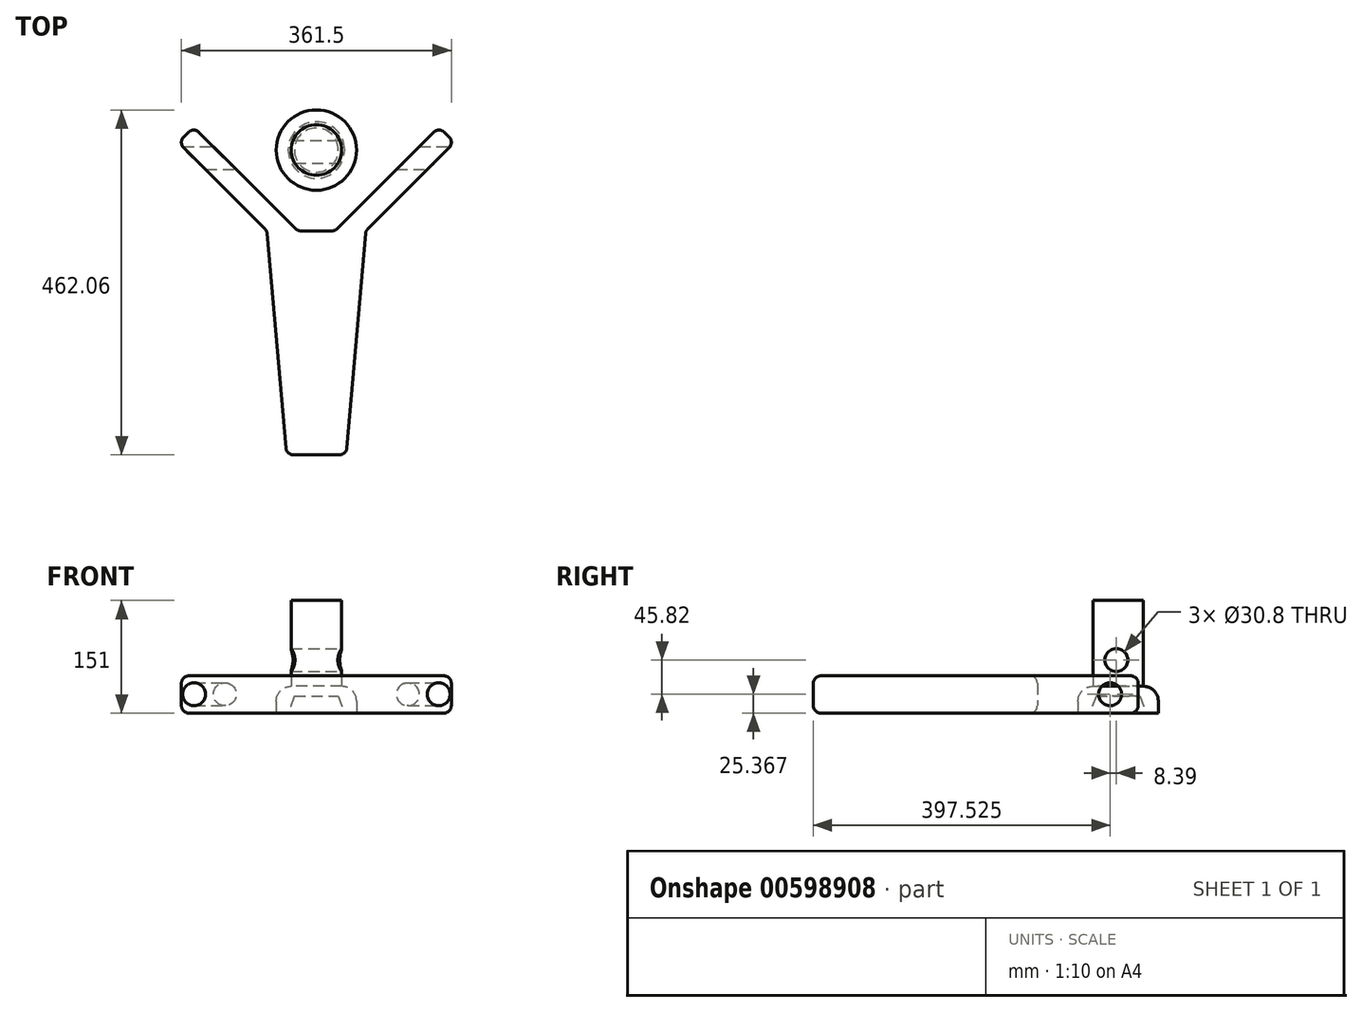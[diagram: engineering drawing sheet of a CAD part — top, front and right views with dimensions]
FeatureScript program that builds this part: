
annotation { "Feature Type Name" : "Feature", "Feature Type Description" : "" }
export const myFeature = defineFeature(function(context is Context, id is Id, definition is map)
    precondition{}
    {
        {
            var Q0;
            Q0=qCreatedBy(makeId("Top.planeOp"),FACE);
            var sketch = newSketch(context, id + "F0", { "sketchPlane" : qUnion([Q0])});
            skLineSegment(sketch, "E0", {"start": v(0, -300) * mm, "end": v(-40, -300) * mm});
            skLineSegment(sketch, "E1", {"start": v(-40, -300) * mm, "end": v(-66.25, 0) * mm});
            skLineSegment(sketch, "E2", {"start": v(-66.25, 0) * mm, "end": v(-184.89, 118.64) * mm});
            skLineSegment(sketch, "E3", {"start": v(-184.89, 118.64) * mm, "end": v(-164.27, 139.27) * mm});
            skLineSegment(sketch, "E4", {"start": v(-164.27, 139.27) * mm, "end": v(-25, 0) * mm});
            skLineSegment(sketch, "E5", {"start": v(-25, 0) * mm, "end": v(0, 0) * mm});
            skLineSegment(sketch, "E6.MirrorCS", {"start": v(25, 0) * mm, "end": v(0, 0) * mm});
            skLineSegment(sketch, "E7.MirrorCS", {"start": v(164.27, 139.27) * mm, "end": v(25, 0) * mm});
            skLineSegment(sketch, "E8.MirrorCS", {"start": v(184.89, 118.64) * mm, "end": v(164.27, 139.27) * mm});
            skLineSegment(sketch, "E9.MirrorCS", {"start": v(66.25, 0) * mm, "end": v(184.89, 118.64) * mm});
            skLineSegment(sketch, "E10.MirrorCS", {"start": v(40, -300) * mm, "end": v(66.25, 0) * mm});
            skLineSegment(sketch, "E11.MirrorCS", {"start": v(0, -300) * mm, "end": v(40, -300) * mm});
            skSolve(sketch);
        }
        {
            var Q0;
            Q0=makeQuery(id+"F0.imprint","IMPRINT",FACE,{"disambiguationData":[TD([[makeQuery(id+"F0.imprint","IMPRINT",EDGE,{"derivedFrom":sQuery(id+"F0.wireOp",EDGE,"E0")}),-1.0]])]});
            extrude(context, id + "F1", {"entities" : qUnion([Q0]), "depth" : 50 * mm, "offsetDistance" : 25 * mm});
        }
        {
            var Q0;
            Q0=makeQuery(id+"F1.opExtrude","SWEPT_FACE",FACE,{"disambiguationData":[OSD([sQuery(id+"F0.wireOp",EDGE,"E2")])]});
            var Q1;
            Q1=makeQuery(id+"F1.opExtrude","SWEPT_FACE",FACE,{"disambiguationData":[OSD([sQuery(id+"F0.wireOp",EDGE,"E1")])]});
            var Q2;
            Q2=makeQuery(id+"F1.opExtrude","SWEPT_FACE",FACE,{"disambiguationData":[OSD([sQuery(id+"F0.wireOp",EDGE,"E0"),sQuery(id+"F0.wireOp",EDGE,"E11.MirrorCS")])]});
            var Q3;
            Q3=makeQuery(id+"F1.opExtrude","SWEPT_EDGE",EDGE,{"disambiguationData":[OSD([sQuery(id+"F0.wireOp",EDGE,"E10.MirrorCS"),sQuery(id+"F0.wireOp",EDGE,"E11.MirrorCS")])]});
            var Q4;
            Q4=makeQuery(id+"F1.opExtrude","SWEPT_FACE",FACE,{"disambiguationData":[OSD([sQuery(id+"F0.wireOp",EDGE,"E10.MirrorCS")])]});
            var Q5;
            Q5=makeQuery(id+"F1.opExtrude","SWEPT_FACE",FACE,{"disambiguationData":[OSD([sQuery(id+"F0.wireOp",EDGE,"E9.MirrorCS")])]});
            var Q6;
            Q6=makeQuery(id+"F1.opExtrude","SWEPT_EDGE",EDGE,{"disambiguationData":[OSD([sQuery(id+"F0.wireOp",EDGE,"E9.MirrorCS"),sQuery(id+"F0.wireOp",EDGE,"E10.MirrorCS")])]});
            var Q7;
            Q7=makeQuery(id+"F1.opExtrude","CAP_EDGE",EDGE,{"disambiguationData":[OSD([sQuery(id+"F0.wireOp",EDGE,"E7.MirrorCS")])],"isStart":true});
            var Q8;
            Q8=makeQuery(id+"F1.opExtrude","CAP_EDGE",EDGE,{"disambiguationData":[OSD([sQuery(id+"F0.wireOp",EDGE,"E9.MirrorCS")])],"isStart":true});
            var Q9;
            Q9=makeQuery(id+"F1.opExtrude","CAP_EDGE",EDGE,{"disambiguationData":[OSD([sQuery(id+"F0.wireOp",EDGE,"E10.MirrorCS")])],"isStart":true});
            var Q10;
            Q10=makeQuery(id+"F1.opExtrude","SWEPT_FACE",FACE,{"disambiguationData":[OSD([sQuery(id+"F0.wireOp",EDGE,"E8.MirrorCS")])]});
            var Q11;
            Q11=makeQuery(id+"F1.opExtrude","SWEPT_FACE",FACE,{"disambiguationData":[OSD([sQuery(id+"F0.wireOp",EDGE,"E7.MirrorCS")])]});
            var Q12;
            Q12=makeQuery(id+"F1.opExtrude","SWEPT_FACE",FACE,{"disambiguationData":[OSD([sQuery(id+"F0.wireOp",EDGE,"E5"),sQuery(id+"F0.wireOp",EDGE,"E6.MirrorCS")])]});
            var Q13;
            Q13=makeQuery(id+"F1.opExtrude","SWEPT_FACE",FACE,{"disambiguationData":[OSD([sQuery(id+"F0.wireOp",EDGE,"E4")])]});
            var Q14;
            Q14=makeQuery(id+"F1.opExtrude","SWEPT_FACE",FACE,{"disambiguationData":[OSD([sQuery(id+"F0.wireOp",EDGE,"E3")])]});
            var Q15;
            Q15=makeQuery(id+"F1.opExtrude","CAP_FACE",FACE,{"disambiguationData":[OSD([sQuery(id+"F0.wireOp",EDGE,"E0"),sQuery(id+"F0.wireOp",EDGE,"E1"),sQuery(id+"F0.wireOp",EDGE,"E2"),sQuery(id+"F0.wireOp",EDGE,"E3"),sQuery(id+"F0.wireOp",EDGE,"E4"),sQuery(id+"F0.wireOp",EDGE,"E5"),sQuery(id+"F0.wireOp",EDGE,"E6.MirrorCS"),sQuery(id+"F0.wireOp",EDGE,"E7.MirrorCS"),sQuery(id+"F0.wireOp",EDGE,"E8.MirrorCS"),sQuery(id+"F0.wireOp",EDGE,"E9.MirrorCS"),sQuery(id+"F0.wireOp",EDGE,"E10.MirrorCS"),sQuery(id+"F0.wireOp",EDGE,"E11.MirrorCS")])],"isStart":false});
            var Q16;
            Q16=makeQuery(id+"F1.opExtrude","CAP_FACE",FACE,{"disambiguationData":[OSD([sQuery(id+"F0.wireOp",EDGE,"E0"),sQuery(id+"F0.wireOp",EDGE,"E1"),sQuery(id+"F0.wireOp",EDGE,"E2"),sQuery(id+"F0.wireOp",EDGE,"E3"),sQuery(id+"F0.wireOp",EDGE,"E4"),sQuery(id+"F0.wireOp",EDGE,"E5"),sQuery(id+"F0.wireOp",EDGE,"E6.MirrorCS"),sQuery(id+"F0.wireOp",EDGE,"E7.MirrorCS"),sQuery(id+"F0.wireOp",EDGE,"E8.MirrorCS"),sQuery(id+"F0.wireOp",EDGE,"E9.MirrorCS"),sQuery(id+"F0.wireOp",EDGE,"E10.MirrorCS"),sQuery(id+"F0.wireOp",EDGE,"E11.MirrorCS")])],"isStart":true});
            var Q17;
            Q17=makeQuery(id+"F1.opExtrude","SWEPT_EDGE",EDGE,{"disambiguationData":[OSD([sQuery(id+"F0.wireOp",EDGE,"E3"),sQuery(id+"F0.wireOp",EDGE,"E4")])]});
            var Q18;
            Q18=makeQuery(id+"F1.opExtrude","CAP_EDGE",EDGE,{"disambiguationData":[OSD([sQuery(id+"F0.wireOp",EDGE,"E1")])],"isStart":false});
            var Q19;
            Q19=makeQuery(id+"F1.opExtrude","CAP_EDGE",EDGE,{"disambiguationData":[OSD([sQuery(id+"F0.wireOp",EDGE,"E2")])],"isStart":false});
            var Q20;
            Q20=makeQuery(id+"F1.opExtrude","CAP_EDGE",EDGE,{"disambiguationData":[OSD([sQuery(id+"F0.wireOp",EDGE,"E2")])],"isStart":true});
            var Q21;
            Q21=makeQuery(id+"F1.opExtrude","SWEPT_EDGE",EDGE,{"disambiguationData":[OSD([sQuery(id+"F0.wireOp",EDGE,"E7.MirrorCS"),sQuery(id+"F0.wireOp",EDGE,"E8.MirrorCS")])]});
            var Q22;
            Q22=makeQuery(id+"F1.opExtrude","SWEPT_EDGE",EDGE,{"disambiguationData":[OSD([sQuery(id+"F0.wireOp",EDGE,"E1"),sQuery(id+"F0.wireOp",EDGE,"E2")])]});
            var Q23;
            Q23=makeQuery(id+"F1.opExtrude","CAP_EDGE",EDGE,{"disambiguationData":[OSD([sQuery(id+"F0.wireOp",EDGE,"E1")])],"isStart":true});
            var Q24;
            Q24=makeQuery(id+"F1.opExtrude","CAP_EDGE",EDGE,{"disambiguationData":[OSD([sQuery(id+"F0.wireOp",EDGE,"E4")])],"isStart":true});
            var Q25;
            Q25=makeQuery(id+"F1.opExtrude","SWEPT_EDGE",EDGE,{"disambiguationData":[OSD([sQuery(id+"F0.wireOp",EDGE,"E2"),sQuery(id+"F0.wireOp",EDGE,"E3")])]});
            var Q26;
            Q26=makeQuery(id+"F1.opExtrude","SWEPT_EDGE",EDGE,{"disambiguationData":[OSD([sQuery(id+"F0.wireOp",EDGE,"E0"),sQuery(id+"F0.wireOp",EDGE,"E1")])]});
            var Q27;
            Q27=makeQuery(id+"F1.opExtrude","CAP_EDGE",EDGE,{"disambiguationData":[OSD([sQuery(id+"F0.wireOp",EDGE,"E10.MirrorCS")])],"isStart":false});
            var Q28;
            Q28=makeQuery(id+"F1.opExtrude","CAP_EDGE",EDGE,{"disambiguationData":[OSD([sQuery(id+"F0.wireOp",EDGE,"E8.MirrorCS")])],"isStart":false});
            var Q29;
            Q29=makeQuery(id+"F1.opExtrude","CAP_EDGE",EDGE,{"disambiguationData":[OSD([sQuery(id+"F0.wireOp",EDGE,"E9.MirrorCS")])],"isStart":false});
            var Q30;
            Q30=makeQuery(id+"F1.opExtrude","SWEPT_EDGE",EDGE,{"disambiguationData":[OSD([sQuery(id+"F0.wireOp",EDGE,"E8.MirrorCS"),sQuery(id+"F0.wireOp",EDGE,"E9.MirrorCS")])]});
            var Q31;
            Q31=makeQuery(id+"F1.opExtrude","CAP_EDGE",EDGE,{"disambiguationData":[OSD([sQuery(id+"F0.wireOp",EDGE,"E0"),sQuery(id+"F0.wireOp",EDGE,"E11.MirrorCS")])],"isStart":true});
            var Q32;
            Q32=makeQuery(id+"F1.opExtrude","CAP_EDGE",EDGE,{"disambiguationData":[OSD([sQuery(id+"F0.wireOp",EDGE,"E5"),sQuery(id+"F0.wireOp",EDGE,"E6.MirrorCS")])],"isStart":false});
            var Q33;
            Q33=makeQuery(id+"F1.opExtrude","CAP_EDGE",EDGE,{"disambiguationData":[OSD([sQuery(id+"F0.wireOp",EDGE,"E4")])],"isStart":false});
            var Q34;
            Q34=makeQuery(id+"F1.opExtrude","CAP_EDGE",EDGE,{"disambiguationData":[OSD([sQuery(id+"F0.wireOp",EDGE,"E3")])],"isStart":false});
            var Q35;
            Q35=makeQuery(id+"F1.opExtrude","SWEPT_EDGE",EDGE,{"disambiguationData":[OSD([sQuery(id+"F0.wireOp",EDGE,"E4"),sQuery(id+"F0.wireOp",EDGE,"E5")])]});
            var Q36;
            Q36=makeQuery(id+"F1.opExtrude","SWEPT_EDGE",EDGE,{"disambiguationData":[OSD([sQuery(id+"F0.wireOp",EDGE,"E6.MirrorCS"),sQuery(id+"F0.wireOp",EDGE,"E7.MirrorCS")])]});
            var Q37;
            Q37=makeQuery(id+"F1.opExtrude","CAP_EDGE",EDGE,{"disambiguationData":[OSD([sQuery(id+"F0.wireOp",EDGE,"E0"),sQuery(id+"F0.wireOp",EDGE,"E11.MirrorCS")])],"isStart":false});
            var Q38;
            Q38=makeQuery(id+"F1.opExtrude","CAP_EDGE",EDGE,{"disambiguationData":[OSD([sQuery(id+"F0.wireOp",EDGE,"E7.MirrorCS")])],"isStart":false});
            var Q39;
            Q39=makeQuery(id+"F1.opExtrude","CAP_EDGE",EDGE,{"disambiguationData":[OSD([sQuery(id+"F0.wireOp",EDGE,"E3")])],"isStart":true});
            var Q40;
            Q40=makeQuery(id+"F1.opExtrude","CAP_EDGE",EDGE,{"disambiguationData":[OSD([sQuery(id+"F0.wireOp",EDGE,"E5"),sQuery(id+"F0.wireOp",EDGE,"E6.MirrorCS")])],"isStart":true});
            var Q41;
            Q41=makeQuery(id+"F1.opExtrude","CAP_EDGE",EDGE,{"disambiguationData":[OSD([sQuery(id+"F0.wireOp",EDGE,"E8.MirrorCS")])],"isStart":true});
            fillet(context, id + "F2", {"entities" : qUnion([Q0, Q1, Q2, Q3, Q4, Q5, Q6, Q7, Q8, Q9, Q10, Q11, Q12, Q13, Q14, Q15, Q16, Q17, Q18, Q19, Q20, Q21, Q22, Q23, Q24, Q25, Q26, Q27, Q28, Q29, Q30, Q31, Q32, Q33, Q34, Q35, Q36, Q37, Q38, Q39, Q40, Q41]), "radius" : 10 * mm, "tangentPropagation" : true, "allowEdgeOverflow" : false});
        }
        {
            var Q0;
            Q0=qCreatedBy(makeId("Right.planeOp"),FACE);
            var sketch = newSketch(context, id + "F3", { "sketchPlane" : qUnion([Q0])});
            skCircle(sketch, "E12", {"center": v(97.52, 25.37) * mm, "radius": 15.4 * mm});
            skSolve(sketch);
        }
        {
            var Q0;
            Q0=makeQuery(id+"F3.imprint","IMPRINT",FACE,{"disambiguationData":[TD([[makeQuery(id+"F3.imprint","IMPRINT",EDGE,{"derivedFrom":sQuery(id+"F3.wireOp",EDGE,"E12")}),1.0]])]});
            extrude(context, id + "F4", {"entities" : qUnion([Q0]), "operationType" : NewBodyOperationType.REMOVE, "oppositeDirection" : true, "depth" : 242.7 * mm, "offsetDistance" : 25 * mm, "hasSecondDirection" : true, "secondDirectionOppositeDirection" : false, "secondDirectionDepth" : 187 * mm});
        }
        {
            var Q0;
            Q0=qCreatedBy(makeId("Top.planeOp"),FACE);
            var sketch = newSketch(context, id + "F5", { "sketchPlane" : qUnion([Q0])});
            skCircle(sketch, "E13", {"center": v(0, 108.26) * mm, "radius": 53.8 * mm});
            skSolve(sketch);
        }
        {
            var Q0;
            Q0=makeQuery(id+"F5.imprint","IMPRINT",FACE,{"disambiguationData":[TD([[makeQuery(id+"F5.imprint","IMPRINT",EDGE,{"derivedFrom":sQuery(id+"F5.wireOp",EDGE,"E13")}),1.0]])]});
            extrude(context, id + "F6", {"entities" : qUnion([Q0]), "depth" : 36 * mm, "offsetDistance" : 25 * mm});
        }
        {
            var Q0;
            Q0=makeQuery(id+"F6.opExtrude","CAP_FACE",FACE,{"disambiguationData":[OSD([sQuery(id+"F5.wireOp",EDGE,"E13")])],"isStart":false});
            fillet(context, id + "F7", {"entities" : qUnion([Q0]), "radius" : 20 * mm, "tangentPropagation" : true, "allowEdgeOverflow" : false});
        }
        {
            var Q0;
            Q0=makeQuery(id+"F6.opExtrude","CAP_FACE",FACE,{"disambiguationData":[OSD([sQuery(id+"F5.wireOp",EDGE,"E13")])],"isStart":false});
            extrude(context, id + "F8", {"entities" : qUnion([Q0]), "operationType" : NewBodyOperationType.ADD, "depth" : 115 * mm, "offsetDistance" : 25 * mm});
        }
        {
            var Q0;
            Q0=qCreatedBy(makeId("Right.planeOp"),FACE);
            var sketch = newSketch(context, id + "F9", { "sketchPlane" : qUnion([Q0])});
            skCircle(sketch, "E14", {"center": v(105.91, 71.19) * mm, "radius": 15.4 * mm});
            skSolve(sketch);
        }
        {
            var Q0;
            Q0 = qSketchRegion(id + "F9", true);
            extrude(context, id + "F10", {"entities" : qUnion([Q0]), "operationType" : NewBodyOperationType.REMOVE, "oppositeDirection" : true, "depth" : 82 * mm, "offsetDistance" : 25 * mm, "hasSecondDirection" : true, "secondDirectionOppositeDirection" : false, "secondDirectionDepth" : 108 * mm});
        }
        {
            var Q0;
            Q0=makeQuery(id+"F6.opExtrude","CAP_FACE",FACE,{"disambiguationData":[OSD([sQuery(id+"F5.wireOp",EDGE,"E13")])],"isStart":true});
            var sketch = newSketch(context, id + "F11", { "sketchPlane" : qUnion([Q0])});
            skCircle(sketch, "E15", {"center": v(0, -108.26) * mm, "radius": 37.84 * mm});
            skSolve(sketch);
        }
        {
            var Q0;
            Q0 = qSketchRegion(id + "F11", true);
            extrude(context, id + "F12", {"entities" : qUnion([Q0]), "operationType" : NewBodyOperationType.REMOVE, "oppositeDirection" : true, "depth" : 23 * mm, "offsetDistance" : 25 * mm, "hasDraft" : true, "draftAngle" : 20 * degree, "draftPullDirection" : true});
        }
    });
